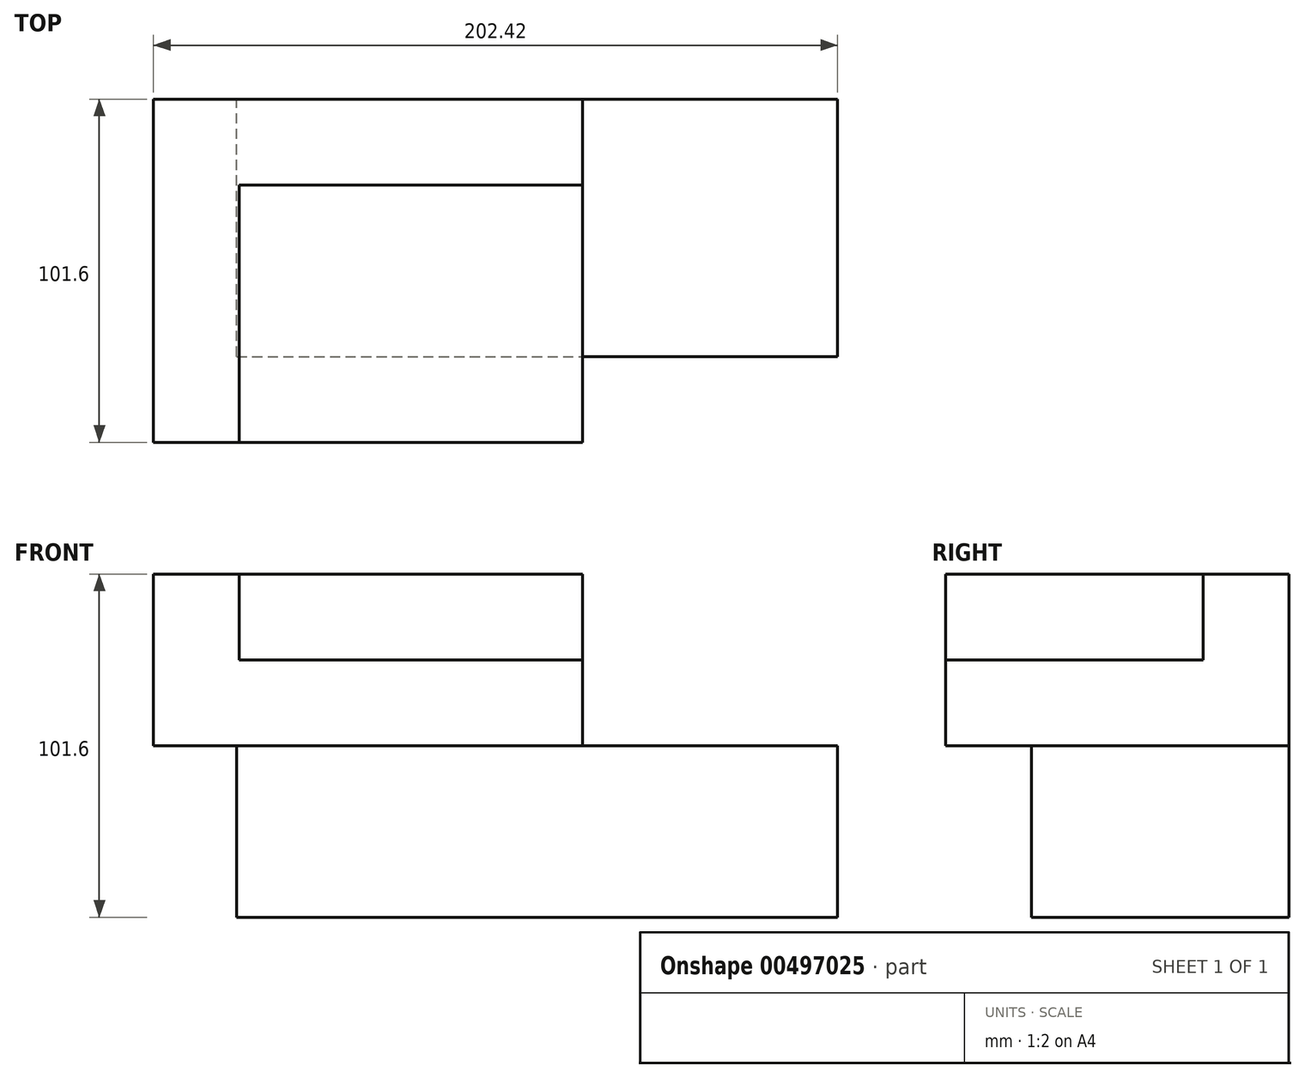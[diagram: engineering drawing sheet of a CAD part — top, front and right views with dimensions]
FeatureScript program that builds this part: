
annotation { "Feature Type Name" : "Feature", "Feature Type Description" : "" }
export const myFeature = defineFeature(function(context is Context, id is Id, definition is map)
    precondition{}
    {
        {
            var Q0;
            Q0=qCreatedBy(makeId("Front.planeOp"),FACE);
            var sketch = newSketch(context, id + "F0", { "sketchPlane" : qUnion([Q0])});
            skLineSegment(sketch, "E0.bottom", {"start": v(0, 0) * mm, "end": v(203.2, 0) * mm});
            skLineSegment(sketch, "E0.top", {"start": v(0, 101.6) * mm, "end": v(203.2, 101.6) * mm});
            skLineSegment(sketch, "E0.left", {"start": v(0, 0) * mm, "end": v(0, 101.6) * mm});
            skLineSegment(sketch, "E0.right", {"start": v(203.2, 0) * mm, "end": v(203.2, 101.6) * mm});
            skSolve(sketch);
        }
        {
            var Q0;
            Q0 = qSketchRegion(id + "F0", true);
            var Q1;
            Q1=makeQuery(id+"F0.imprint","IMPRINT",FACE,{"disambiguationData":[TD([[makeQuery(id+"F0.imprint","IMPRINT",EDGE,{"derivedFrom":sQuery(id+"F0.wireOp",EDGE,"E0.bottom")}),1.0]])]});
            extrude(context, id + "F1", {"entities" : qUnion([Q0, Q1]), "depth" : 76.2 * mm});
        }
        {
            var Q0;
            Q0=makeQuery(id+"F1.opExtrude","SWEPT_FACE",FACE,{"disambiguationData":[OSD([sQuery(id+"F0.wireOp",EDGE,"E0.top")])]});
            extrude(context, id + "F2", {"entities" : qUnion([Q0]), "operationType" : NewBodyOperationType.REMOVE, "oppositeDirection" : true, "depth" : 50.8 * mm});
        }
        {
            var Q0;
            Q0=makeQuery(id+"F2.boolean.opBoolean","COPY",FACE,{"derivedFrom":makeQuery(id+"F2.opExtrude","CAP_FACE",FACE,{"disambiguationData":[OSD([sQuery(id+"F0.wireOp",EDGE,"E0.top")])],"isStart":false})});
            var sketch = newSketch(context, id + "F3", { "sketchPlane" : qUnion([Q0])});
            skLineSegment(sketch, "E1.bottom", {"start": v(-24.62, -101.6) * mm, "end": v(102.38, -101.6) * mm});
            skLineSegment(sketch, "E1.top", {"start": v(-24.62, 0) * mm, "end": v(102.38, 0) * mm});
            skLineSegment(sketch, "E1.left", {"start": v(-24.62, -101.6) * mm, "end": v(-24.62, 0) * mm});
            skLineSegment(sketch, "E1.right", {"start": v(102.38, -101.6) * mm, "end": v(102.38, 0) * mm});
            skSolve(sketch);
        }
        {
            var Q0;
            Q0 = qSketchRegion(id + "F3", true);
            extrude(context, id + "F4", {"entities" : qUnion([Q0]), "operationType" : NewBodyOperationType.ADD, "depth" : 50.8 * mm});
        }
        {
            var Q0;
            Q0=makeQuery(id+"F1.opExtrude","SWEPT_FACE",FACE,{"disambiguationData":[OSD([sQuery(id+"F0.wireOp",EDGE,"E0.right")])]});
            extrude(context, id + "F5", {"entities" : qUnion([Q0]), "operationType" : NewBodyOperationType.ADD, "oppositeDirection" : true, "depth" : 25.4 * mm});
        }
        {
            var Q0;
            Q0=makeQuery(id+"F1.opExtrude","SWEPT_FACE",FACE,{"disambiguationData":[OSD([sQuery(id+"F0.wireOp",EDGE,"E0.right")])]});
            extrude(context, id + "F6", {"entities" : qUnion([Q0]), "operationType" : NewBodyOperationType.REMOVE, "oppositeDirection" : true, "depth" : 25.4 * mm});
        }
        {
            var Q0;
            Q0=makeQuery(id+"F4.opExtrude","CAP_FACE",FACE,{"disambiguationData":[OSD([sQuery(id+"F3.wireOp",EDGE,"E1.bottom"),sQuery(id+"F3.wireOp",EDGE,"E1.top"),sQuery(id+"F3.wireOp",EDGE,"E1.left"),sQuery(id+"F3.wireOp",EDGE,"E1.right")])],"isStart":false});
            var sketch = newSketch(context, id + "F7", { "sketchPlane" : qUnion([Q0])});
            skLineSegment(sketch, "E2", {"start": v(0.78, -101.6) * mm, "end": v(0.78, -25.4) * mm});
            skLineSegment(sketch, "E3", {"start": v(0.78, -25.4) * mm, "end": v(102.38, -25.4) * mm});
            skSolve(sketch);
        }
        {
            var Q0;
            {var subQ0=sQuery(id+"F7.wireOp",EDGE,"E2");Q0=makeQuery(id+"F7.imprint","IMPRINT",FACE,{"disambiguationData":[TD([[makeQuery(id+"F7.imprint","IMPRINT",EDGE,{"derivedFrom":subQ0}),-1.0]])]});}
            extrude(context, id + "F8", {"entities" : qUnion([Q0]), "operationType" : NewBodyOperationType.REMOVE, "oppositeDirection" : true, "depth" : 25.4 * mm});
        }
    });
